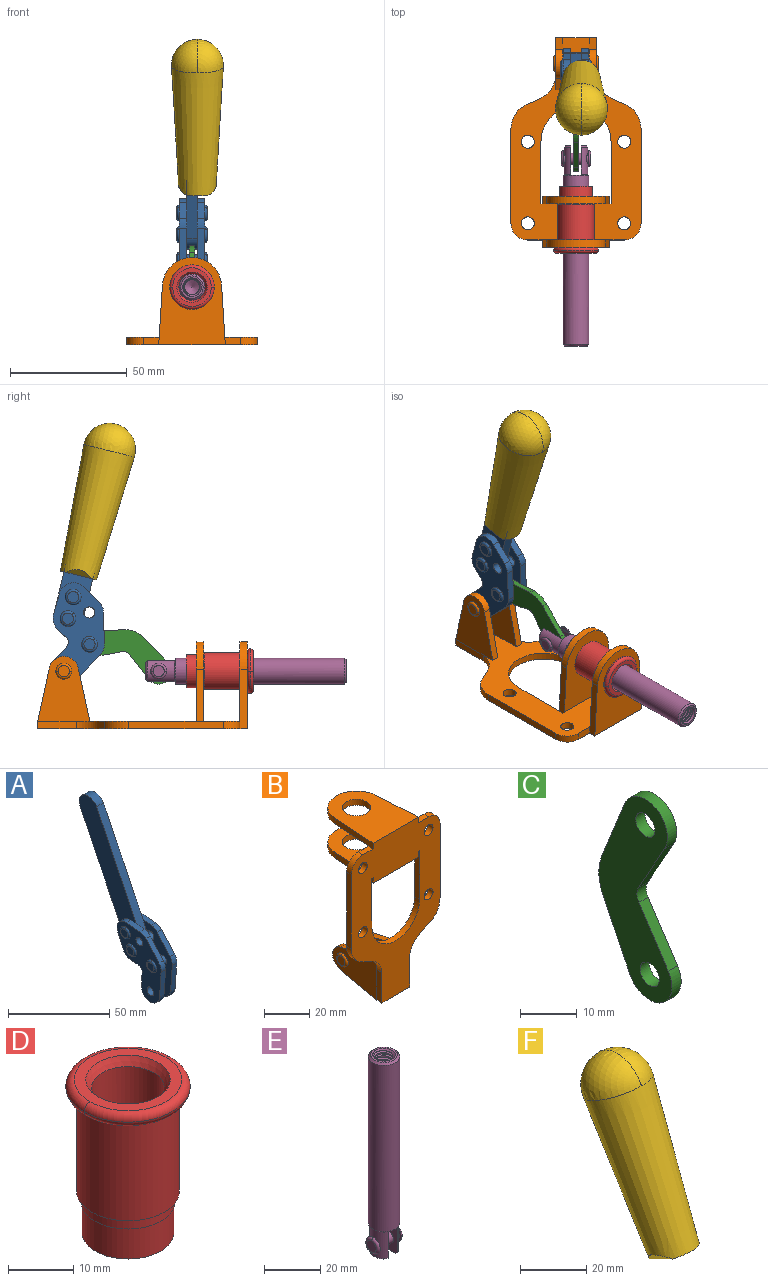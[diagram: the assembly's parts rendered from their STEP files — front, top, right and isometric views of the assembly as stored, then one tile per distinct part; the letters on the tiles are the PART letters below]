
ASSEMBLY  parts=6 mates=6
PART A: 59 faces, bbox 12.9x60.2x99.6 mm
  f0: torus R=2.39mm, axis (-1,0,0), area 14.9mm2, adj f20,f43,f51
  f1: torus R=2.39mm, axis (-1,0,0), area 14.9mm2, adj f19,f42,f51
  f2: torus R=2.39mm, axis (-1,0,0), area 14.9mm2, adj f18,f35,f51
  f3: torus R=2.39mm, axis (-1,0,0), area 14.9mm2, adj f14,f17,f23
  f4: torus R=2.39mm, axis (-1,0,0), area 14.9mm2, adj f13,f16,f23
  f5: torus R=2.39mm, axis (-1,0,0), area 14.9mm2, adj f12,f15,f23
  f6: cylinder r=2.39mm len=4.78mm, axis (1,0,0), area 46.5mm2, adj f48,f50,f51
  f7: cylinder r=2.39mm len=4.78mm, axis (1,0,0), area 46.5mm2, adj f50,f51
  f8: cylinder r=6.35mm len=12.68mm, axis (1,0,0), area 61.8mm2, adj f38,f39,f50,f51
  f9: cylinder r=2.39mm len=4.78mm, axis (-1,0,0), area 70.5mm2, adj f46,f50
  f10: cylinder r=2.39mm len=4.78mm, axis (-1,0,0), area 46.5mm2, adj f23,f45,f46
  f11: cylinder r=2.39mm len=4.78mm, axis (-1,0,0), area 46.5mm2, adj f23,f46
  f12: plane 4.78x4.78mm, normal (1,0,0), area 17.9mm2, adj f5,f15
  f13: plane 4.78x4.78mm, normal (1,0,0), area 17.9mm2, adj f4,f16
  f14: plane 4.78x4.78mm, normal (1,0,0), area 17.9mm2, adj f3,f17
  f15: torus R=2.39mm, axis (-1,0,0), area 14.9mm2, adj f5,f12,f23
  f16: torus R=2.39mm, axis (-1,0,0), area 14.9mm2, adj f4,f13,f23
  f17: torus R=2.39mm, axis (-1,0,0), area 14.9mm2, adj f3,f14,f23
  f18: plane 4.78x4.78mm, normal (-1,0,0), area 17.9mm2, adj f2,f35
  f19: plane 4.78x4.78mm, normal (-1,0,0), area 17.9mm2, adj f1,f42
  f20: plane 4.78x4.78mm, normal (-1,0,0), area 17.9mm2, adj f0,f43
  f21: plane 2.26x0.2mm, normal (1,0,0), area 0.2mm2, adj f31,f44
  f22: plane 2.26x0.2mm, normal (-1,0,0), area 0.2mm2, adj f41,f44
  f23: plane 39.37x30.77mm, normal (1,0,0), area 565.5mm2, adj f3,f4,f5,f10,f11,f15,f16,f17
  f24: cylinder r=6.1mm len=4.15mm, axis (-1,0,0), area 14.7mm2, adj f23,f25,f32,f46
  f25: plane 10.25x9.01mm, normal (0,-0.75,0.66), area 42.3mm2, adj f23,f24,f26,f46
  f26: cylinder r=6.35mm len=4.64mm, axis (-1,0,0), area 15.6mm2, adj f23,f25,f27,f46
  f27: plane 15.84x3.1mm, normal (0,-1,-0.07), area 49.2mm2, adj f23,f26,f28,f46
  f28: cylinder r=6.35mm len=12.68mm, axis (-1,0,0), area 61.8mm2, adj f23,f27,f29,f46
  f29: plane 8.11x3.1mm, normal (0,1,0.07), area 25.2mm2, adj f23,f28,f30,f46
  f30: cylinder r=3.05mm len=3.25mm, axis (-1,0,0), area 14.8mm2, adj f23,f29,f31,f46
  f31: plane 5.99x3.1mm, normal (0,0.07,-1), area 18.6mm2, adj f21,f23,f30,f44,f46
  f32: plane 9.5x3.1mm, normal (0,-0.07,1), area 29.5mm2, adj f23,f24,f33,f46,f47
  f33: cylinder r=6.1mm len=8.63mm, axis (-1,0,0), area 39.1mm2, adj f23,f32,f34,f47
  f34: plane 8.65x3.96mm, normal (0,0.91,-0.42), area 29.5mm2, adj f23,f33,f44,f47
  f35: torus R=2.39mm, axis (-1,0,0), area 14.9mm2, adj f2,f18,f51
  f36: plane 10.25x9.01mm, normal (0,-0.75,0.66), area 42.3mm2, adj f37,f49,f50,f51
  f37: cylinder r=6.35mm len=4.64mm, axis (1,0,0), area 15.6mm2, adj f36,f38,f50,f51
  f38: plane 15.84x3.1mm, normal (0,-1,-0.07), area 49.2mm2, adj f8,f37,f50,f51
  f39: plane 8.11x3.1mm, normal (0,1,0.07), area 25.2mm2, adj f8,f40,f50,f51
  f40: cylinder r=3.05mm len=3.25mm, axis (1,0,0), area 14.8mm2, adj f39,f41,f50,f51
  f41: plane 5.99x3.1mm, normal (0,0.07,-1), area 18.6mm2, adj f22,f40,f44,f50,f51
  f42: torus R=2.39mm, axis (-1,0,0), area 14.9mm2, adj f1,f19,f51
  f43: torus R=2.39mm, axis (-1,0,0), area 14.9mm2, adj f0,f20,f51
  f44: cylinder r=6.35mm len=12.12mm, axis (-1,0,0), area 128.9mm2, adj f21,f22,f23,f31,f34,f41,f46,f47
  f45: plane 2.65x1.35mm, normal (1,0,0), area 1mm2, adj f10,f55
  f46: plane 39.08x20.42mm, normal (-1,0,0), area 412.5mm2, adj f9,f10,f11,f24,f25,f26,f27,f28
  f47: plane 77.62x39.82mm, normal (1,0,0), area 850mm2, adj f32,f33,f34,f44,f53,f54,f55
  f48: plane 2.65x1.35mm, normal (-1,0,0), area 1mm2, adj f6,f55
  f49: cylinder r=6.1mm len=4.15mm, axis (1,0,0), area 14.7mm2, adj f36,f50,f51,f56
  f50: plane 39.08x20.42mm, normal (1,0,0), area 412.5mm2, adj f6,f7,f8,f9,f36,f37,f38,f39
  f51: plane 39.37x30.77mm, normal (-1,0,0), area 565.5mm2, adj f0,f1,f2,f6,f7,f8,f35,f36
  f52: plane 8.65x3.96mm, normal (0,0.91,-0.42), area 29.5mm2, adj f44,f51,f57,f58
  f53: plane 68.49x33.4mm, normal (0,0.9,-0.44), area 358.1mm2, adj f44,f47,f54,f58
  f54: cylinder r=6.35mm len=12.06mm, axis (1,0,0), area 93.7mm2, adj f47,f53,f55,f58
  f55: plane 68.49x33.4mm, normal (0,-0.9,0.44), area 358.1mm2, adj f44,f45,f46,f47,f48,f50,f54,f58
  f56: plane 9.5x3.1mm, normal (0,-0.07,1), area 29.5mm2, adj f49,f50,f51,f57,f58
  f57: cylinder r=6.1mm len=8.63mm, axis (1,0,0), area 39.1mm2, adj f51,f52,f56,f58
  f58: plane 77.62x39.82mm, normal (-1,0,0), area 850mm2, adj f44,f52,f53,f54,f55,f56,f57
PART B: 55 faces, bbox 55.7x37.4x89.8 mm
  f0: torus R=2.41mm, axis (-1,0,0), area 15mm2, adj f11,f15,f25
  f1: torus R=2.41mm, axis (-1,0,0), area 15mm2, adj f10,f12,f22
  f2: cylinder r=2.78mm len=5.56mm, axis (0,-1,0), area 54.2mm2, adj f30,f54
  f3: cylinder r=14.99mm len=29.97mm, axis (0,-1,0), area 145.9mm2, adj f30,f49,f53,f54
  f4: cylinder r=2.78mm len=5.56mm, axis (0,-1,0), area 54.2mm2, adj f30,f54
  f5: cylinder r=2.78mm len=5.56mm, axis (0,-1,0), area 54.2mm2, adj f30,f54
  f6: cylinder r=2.78mm len=5.56mm, axis (0,-1,0), area 54.2mm2, adj f30,f54
  f7: cylinder r=6.35mm len=12.7mm, axis (0,0,1), area 123.6mm2, adj f27,f51
  f8: cylinder r=6.35mm len=12.7mm, axis (0,0,-1), area 124.7mm2, adj f21,f35
  f9: cylinder r=2.41mm len=11.18mm, axis (-1,0,0), area 169.4mm2, adj f16,f19
  f10: plane 4.83x4.83mm, normal (1,0,0), area 18.3mm2, adj f1,f12
  f11: plane 4.83x4.83mm, normal (-1,0,0), area 18.3mm2, adj f0,f15
  f12: torus R=2.41mm, axis (-1,0,0), area 15mm2, adj f1,f10,f22
  f13: cylinder r=6.35mm len=12.41mm, axis (1,0,0), area 53.4mm2, adj f18,f19,f22,f23
  f14: cylinder r=6.35mm len=12.41mm, axis (-1,0,0), area 53.4mm2, adj f16,f17,f24,f25
  f15: torus R=2.41mm, axis (-1,0,0), area 15mm2, adj f0,f11,f25
  f16: plane 27.86x22.35mm, normal (1,0,0), area 425.4mm2, adj f9,f14,f17,f24,f30
  f17: plane 22.86x4.97mm, normal (0,0.21,0.98), area 72.5mm2, adj f14,f16,f25,f30
  f18: plane 22.86x4.97mm, normal (0,0.21,0.98), area 72.5mm2, adj f13,f19,f22,f30
  f19: plane 27.86x22.35mm, normal (-1,0,0), area 425.4mm2, adj f9,f13,f18,f23,f30
  f20: cylinder r=12.7mm len=25.35mm, axis (0,0,-1), area 119.8mm2, adj f21,f34,f35,f36
  f21: plane 34.21x28.07mm, normal (0,0,-1), area 702.4mm2, adj f8,f20,f30,f34,f36
  f22: plane 27.96x22.45mm, normal (1,0,0), area 407.2mm2, adj f1,f12,f13,f18,f23,f30,f42,f43
  f23: plane 22.86x4.97mm, normal (0,0.21,-0.98), area 72.5mm2, adj f13,f19,f22,f44
  f24: plane 22.86x4.97mm, normal (0,0.21,-0.98), area 72.5mm2, adj f14,f16,f25,f44
  f25: plane 27.86x22.35mm, normal (-1,0,0), area 407.1mm2, adj f0,f14,f15,f17,f24,f30,f45,f46
  f26: plane 3.1x0.95mm, normal (0,0,-1), area 2.7mm2, adj f30,f49,f50,f54
  f27: plane 34.21x28.07mm, normal (0,0,1), area 702.4mm2, adj f7,f28,f30,f50,f52
  f28: cylinder r=12.7mm len=25.35mm, axis (0,0,1), area 118.8mm2, adj f27,f50,f51,f52
  f29: plane 3.1x0.95mm, normal (0,0,-1), area 2.7mm2, adj f30,f52,f53,f54
  f30: plane 86.54x55.63mm, normal (0,1,0), area 2362.9mm2, adj f2,f3,f4,f5,f6,f16,f17,f18
  f31: plane 40.56x3.1mm, normal (-1,0,0), area 125.7mm2, adj f30,f32,f48,f54
  f32: cylinder r=7.11mm len=7.11mm, axis (0,-1,0), area 34.6mm2, adj f30,f31,f33,f54
  f33: plane 6.67x3.1mm, normal (0,0,1), area 20.4mm2, adj f30,f32,f34,f54
  f34: plane 25.39x3.13mm, normal (-1,0.06,0), area 79.5mm2, adj f20,f21,f33,f35,f54
  f35: plane 37.31x28.45mm, normal (0,0,1), area 789.9mm2, adj f8,f20,f34,f36,f54
  f36: plane 25.39x3.13mm, normal (1,0.06,0), area 79.5mm2, adj f20,f21,f35,f37,f54
  f37: plane 6.67x3.1mm, normal (0,0,1), area 20.4mm2, adj f30,f36,f38,f54
  f38: cylinder r=7.11mm len=7.11mm, axis (0,-1,0), area 34.6mm2, adj f30,f37,f39,f54
  f39: plane 40.56x3.1mm, normal (1,0,0), area 125.7mm2, adj f30,f38,f40,f54
  f40: cylinder r=11.18mm len=10.16mm, axis (0,-1,0), area 39.5mm2, adj f30,f39,f41,f54
  f41: plane 6.09x3.1mm, normal (0.42,0,-0.91), area 20.8mm2, adj f30,f40,f42,f54
  f42: cylinder r=11.18mm len=9.41mm, axis (0,-1,0), area 37.2mm2, adj f22,f30,f41,f43,f54
  f43: plane 16.5x3.1mm, normal (1,0,0), area 51.1mm2, adj f22,f42,f44,f54
  f44: plane 17.37x3.1mm, normal (0,0,-1), area 53.8mm2, adj f23,f24,f30,f43,f45,f54
  f45: plane 16.5x3.1mm, normal (-1,0,0), area 51.1mm2, adj f25,f44,f46,f54
  f46: cylinder r=11.18mm len=9.41mm, axis (0,-1,0), area 37.2mm2, adj f25,f30,f45,f47,f54
  f47: plane 6.09x3.1mm, normal (-0.42,0,-0.91), area 20.8mm2, adj f30,f46,f48,f54
  f48: cylinder r=11.18mm len=10.16mm, axis (0,-1,0), area 39.5mm2, adj f30,f31,f47,f54
  f49: plane 26.54x3.1mm, normal (-1,0,0), area 82.3mm2, adj f3,f26,f30,f54
  f50: plane 25.39x3.1mm, normal (1,0.06,0), area 78.8mm2, adj f26,f27,f28,f51,f54
  f51: plane 37.31x28.45mm, normal (0,0,-1), area 789.9mm2, adj f7,f28,f50,f52,f54
  f52: plane 25.39x3.1mm, normal (-1,0.06,0), area 78.8mm2, adj f27,f28,f29,f51,f54
  f53: plane 26.54x3.1mm, normal (1,0,0), area 82.3mm2, adj f3,f29,f30,f54
  f54: plane 89.66x55.63mm, normal (0,-1,0), area 2678.5mm2, adj f2,f3,f4,f5,f6,f26,f29,f31
PART C: 12 faces, bbox 2.3x18.2x42.8 mm
  f0: cylinder r=2.4mm len=4.8mm, axis (1,0,0), area 34.9mm2, adj f4,f11
  f1: cylinder r=10.41mm len=8.47mm, axis (1,0,0), area 20.2mm2, adj f4,f9,f10,f11
  f2: cylinder r=3.05mm len=3.16mm, axis (1,0,0), area 7.7mm2, adj f4,f6,f7,f11
  f3: cylinder r=2.4mm len=4.8mm, axis (1,0,0), area 34.9mm2, adj f4,f11
  f4: plane 42.81x18.23mm, normal (-1,0,0), area 414.1mm2, adj f0,f1,f2,f3,f5,f6,f7,f8
  f5: cylinder r=5.54mm len=10.67mm, axis (1,0,0), area 41.8mm2, adj f4,f6,f10,f11
  f6: plane 11.66x6.53mm, normal (0,-0.87,-0.49), area 30.9mm2, adj f2,f4,f5,f11
  f7: plane 11.17x7.33mm, normal (0,-0.84,0.55), area 30.9mm2, adj f2,f4,f8,f11
  f8: cylinder r=5.54mm len=10.51mm, axis (1,0,0), area 41.8mm2, adj f4,f7,f9,f11
  f9: plane 13.67x6.67mm, normal (0,0.9,-0.44), area 35.1mm2, adj f1,f4,f8,f11
  f10: plane 14.1x5.7mm, normal (0,0.93,0.37), area 35.1mm2, adj f1,f4,f5,f11
  f11: plane 42.81x18.23mm, normal (1,0,0), area 414.1mm2, adj f0,f1,f2,f3,f5,f6,f7,f8
PART D: 15 faces, bbox 20.6x20.6x28.7 mm
  f0: torus R=8.26mm, axis (0,0,1), area 56.8mm2, adj f1,f10,f12
  f1: torus R=8.26mm, axis (0,0,1), area 56.8mm2, adj f0,f6,f13
  f2: cylinder r=5.59mm len=25.91mm, axis (0,0,1), area 909.6mm2, adj f3,f4
  f3: cone r=6.86mm half-angle=45deg, axis (0,0,-1), area 70.2mm2, adj f2,f14
  f4: cone r=6.47mm half-angle=30deg, axis (0,0,1), area 66.7mm2, adj f2,f13
  f5: cylinder r=7.04mm len=14.07mm, axis (0,0,1), area 252.6mm2, adj f11,f14
  f6: torus R=8.26mm, axis (0,0,1), area 56.8mm2, adj f1,f12,f13
  f7: cylinder r=7.16mm len=14.33mm, axis (0,0,1), area 91.5mm2, adj f9,f11
  f8: cylinder r=7.86mm len=18.42mm, axis (0,0,1), area 909.6mm2, adj f9,f10
  f9: plane 15.72x15.72mm, normal (0,0,-1), area 33mm2, adj f7,f8
  f10: plane 16.51x16.51mm, normal (0,0,-1), area 19.9mm2, adj f0,f8,f12
  f11: plane 14.33x14.33mm, normal (0,0,-1), area 5.7mm2, adj f5,f7
  f12: torus R=8.26mm, axis (0,0,1), area 56.8mm2, adj f0,f6,f10
  f13: plane 16.51x16.51mm, normal (0,0,1), area 82.7mm2, adj f1,f4,f6
  f14: plane 14.07x14.07mm, normal (0,0,-1), area 7.8mm2, adj f3,f5
PART E: 48 faces, bbox 12.6x11.1x86.1 mm
  f0: torus R=2.41mm, axis (-1,0,0), area 15mm2, adj f30,f32,f34
  f1: torus R=2.41mm, axis (-1,0,0), area 15mm2, adj f29,f31,f33
  f2: cylinder r=5.54mm len=72.39mm, axis (0,0,1), area 2518.5mm2, adj f3,f4,f42,f43
  f3: cone r=5.54mm half-angle=45deg, axis (0,0,1), area 7.6mm2, adj f2,f5,f41
  f4: cone r=5.54mm half-angle=45deg, axis (0,0,-1), area 34.9mm2, adj f2,f39
  f5: cylinder r=5.08mm len=11.48mm, axis (0,0,1), area 108.3mm2, adj f3,f7,f8,f41
  f6: cylinder r=2.41mm len=4.83mm, axis (-1,0,0), area 71.2mm2, adj f40,f41
  f7: cylinder r=2.41mm len=4.83mm, axis (-1,0,0), area 7.6mm2, adj f5,f34
  f8: cone r=5.08mm half-angle=45deg, axis (0,0,1), area 10.6mm2, adj f5,f37,f41
  f9: cone r=3.98mm half-angle=45deg, axis (0,0,1), area 17.6mm2, adj f27,f39,f45,f46,f47
  f10: cylinder r=2.41mm len=4.83mm, axis (-1,0,0), area 7.6mm2, adj f33,f38
  f11: cylinder r=3.2mm len=6.4mm, axis (0,0,1), area 78.4mm2, adj f12,f28,f44,f45,f47
  f12: cylinder r=3.2mm len=6.4mm, axis (0,0,1), area 10.5mm2, adj f11,f13,f45,f47
  f13: cylinder r=3.2mm len=6.4mm, axis (0,0,1), area 10.5mm2, adj f12,f14,f45,f47
  f14: cylinder r=3.2mm len=6.4mm, axis (0,0,1), area 10.5mm2, adj f13,f15,f45,f47
  f15: cylinder r=3.2mm len=6.4mm, axis (0,0,1), area 10.5mm2, adj f14,f16,f45,f47
  f16: cylinder r=3.2mm len=6.4mm, axis (0,0,1), area 10.5mm2, adj f15,f17,f45,f47
  f17: cylinder r=3.2mm len=6.4mm, axis (0,0,1), area 10.5mm2, adj f16,f18,f45,f47
  f18: cylinder r=3.2mm len=6.4mm, axis (0,0,1), area 10.5mm2, adj f17,f19,f45,f47
  f19: cylinder r=3.2mm len=6.4mm, axis (0,0,1), area 10.5mm2, adj f18,f20,f45,f47
  f20: cylinder r=3.2mm len=6.4mm, axis (0,0,1), area 10.5mm2, adj f19,f21,f45,f47
  f21: cylinder r=3.2mm len=6.4mm, axis (0,0,1), area 10.5mm2, adj f20,f22,f45,f47
  f22: cylinder r=3.2mm len=6.4mm, axis (0,0,1), area 10.5mm2, adj f21,f23,f45,f47
  f23: cylinder r=3.2mm len=6.4mm, axis (0,0,1), area 10.5mm2, adj f22,f24,f45,f47
  f24: cylinder r=3.2mm len=6.4mm, axis (0,0,1), area 10.5mm2, adj f23,f25,f45,f47
  f25: cylinder r=3.2mm len=6.4mm, axis (0,0,1), area 10.5mm2, adj f24,f26,f45,f47
  f26: cylinder r=3.2mm len=6.4mm, axis (0,0,1), area 10.5mm2, adj f25,f27,f45,f47
  f27: cylinder r=3.2mm len=6.4mm, axis (0,0,1), area 7.4mm2, adj f9,f26,f45,f47
  f28: cone r=3.2mm half-angle=60deg, axis (0,0,1), area 37.2mm2, adj f11
  f29: plane 4.83x4.83mm, normal (-1,0,0), area 18.3mm2, adj f1,f31
  f30: plane 4.83x4.83mm, normal (1,0,0), area 18.3mm2, adj f0,f32
  f31: torus R=2.41mm, axis (-1,0,0), area 15mm2, adj f1,f29,f33
  f32: torus R=2.41mm, axis (-1,0,0), area 15mm2, adj f0,f30,f34
  f33: plane 6.83x6.83mm, normal (1,0,0), area 18.3mm2, adj f1,f10,f31
  f34: plane 6.83x6.83mm, normal (-1,0,0), area 18.3mm2, adj f0,f7,f32
  f35: cone r=5.08mm half-angle=45deg, axis (0,0,1), area 10.6mm2, adj f36,f38,f40
  f36: plane 7.25x1.97mm, normal (0,0,-1), area 10mm2, adj f35,f40
  f37: plane 7.25x1.97mm, normal (0,0,-1), area 10mm2, adj f8,f41
  f38: cylinder r=5.08mm len=11.48mm, axis (0,0,1), area 108.3mm2, adj f10,f35,f40,f42
  f39: plane 9.55x9.55mm, normal (0,0,1), area 22mm2, adj f4,f9
  f40: plane 12.76x10.09mm, normal (1,0,0), area 95.7mm2, adj f6,f35,f36,f38,f42,f43
  f41: plane 12.76x10.09mm, normal (-1,0,0), area 95.7mm2, adj f3,f5,f6,f8,f37,f43
  f42: cone r=5.54mm half-angle=45deg, axis (0,0,1), area 7.6mm2, adj f2,f38,f40
  f43: plane 11.07x4.7mm, normal (0,0,-1), area 50.4mm2, adj f2,f40,f41
  f44: plane 0.89x0.62mm, normal (-1,0,0), area 0.3mm2, adj f11,f45,f46,f47
  f45: bspline ~24.8x7.63mm, area 266.6mm2, adj f9,f11,f12,f13,f14,f15,f16,f17
  f46: bspline ~24.87x7.63mm, area 73.6mm2, adj f9,f44,f45,f47
  f47: bspline ~24.98x7.63mm, area 272.5mm2, adj f9,f11,f12,f13,f14,f15,f16,f17
PART F: 11 faces, bbox 22.3x42.6x64.5 mm
  f0: sphere r=11.13mm, area 411.4mm2, adj f1,f8
  f1: cone r=11.11mm half-angle=3.3deg, axis (0,0.44,0.9), area 3251.8mm2, adj f0,f7,f8,f9,f10
  f2: cylinder r=6.16mm len=11.7mm, axis (1,0,0), area 89.5mm2, adj f3,f4,f5,f6
  f3: plane 60.23x36.75mm, normal (-1,0,0), area 763.6mm2, adj f2,f4,f6,f10
  f4: plane 51.37x25.05mm, normal (0,0.9,-0.44), area 264.2mm2, adj f2,f3,f5,f10
  f5: plane 60.23x36.75mm, normal (1,0,0), area 763.6mm2, adj f2,f4,f6,f10
  f6: plane 51.37x25.05mm, normal (0,-0.9,0.44), area 264.2mm2, adj f2,f3,f5,f10
  f7: plane 9.95x5.95mm, normal (0.71,-0.31,-0.64), area 25.8mm2, adj f1,f10
  f8: sphere r=11.13mm, area 411.4mm2, adj f0,f1
  f9: plane 9.95x5.95mm, normal (-0.71,-0.31,-0.64), area 25.8mm2, adj f1,f10
  f10: plane 14.27x11.38mm, normal (0,-0.44,-0.9), area 106.7mm2, adj f1,f3,f4,f5,f6,f7,f9
PLACE A rot(axis=(1,0,0),39.8deg) t=(0,2.07,33.51)mm
PLACE B rot(axis=(1,0,0),90deg) t=(0,9.43,0)mm fixed
PLACE C rot(axis=(1,0,0),113.2deg) t=(0,24.83,8.07)mm
PLACE D rot(axis=(1,0,0),90deg) t=(0,9.43,0)mm
PLACE E rot(axis=(1,0,0),90deg) t=(0,16.4,0)mm
PLACE F rot(axis=(1,0,0),39.8deg) t=(2.31,2.07,33.51)mm
MATE revolute A.f7 <-> B.f0  axis (-1,0,0) through (0,41.52,24.61)mm
MATE revolute E.f6 <-> C.f5  axis (-1,0,0) through (0,0.92,24.61)mm
MATE revolute A.f4 <-> C.f3  axis (-1,0,0) through (0,30.53,36.07)mm
MATE fastened A.f54 <-> F.f2  axis (1,0,0) through (0,21.58,121.07)mm
MATE fastened B.f7 <-> D.f2  axis (0,-1,0) through (0,-36.96,24.61)mm
MATE slider E.f2 <-> B.f7  axis (0,-1,0) through (0,-42.38,24.61)mm
